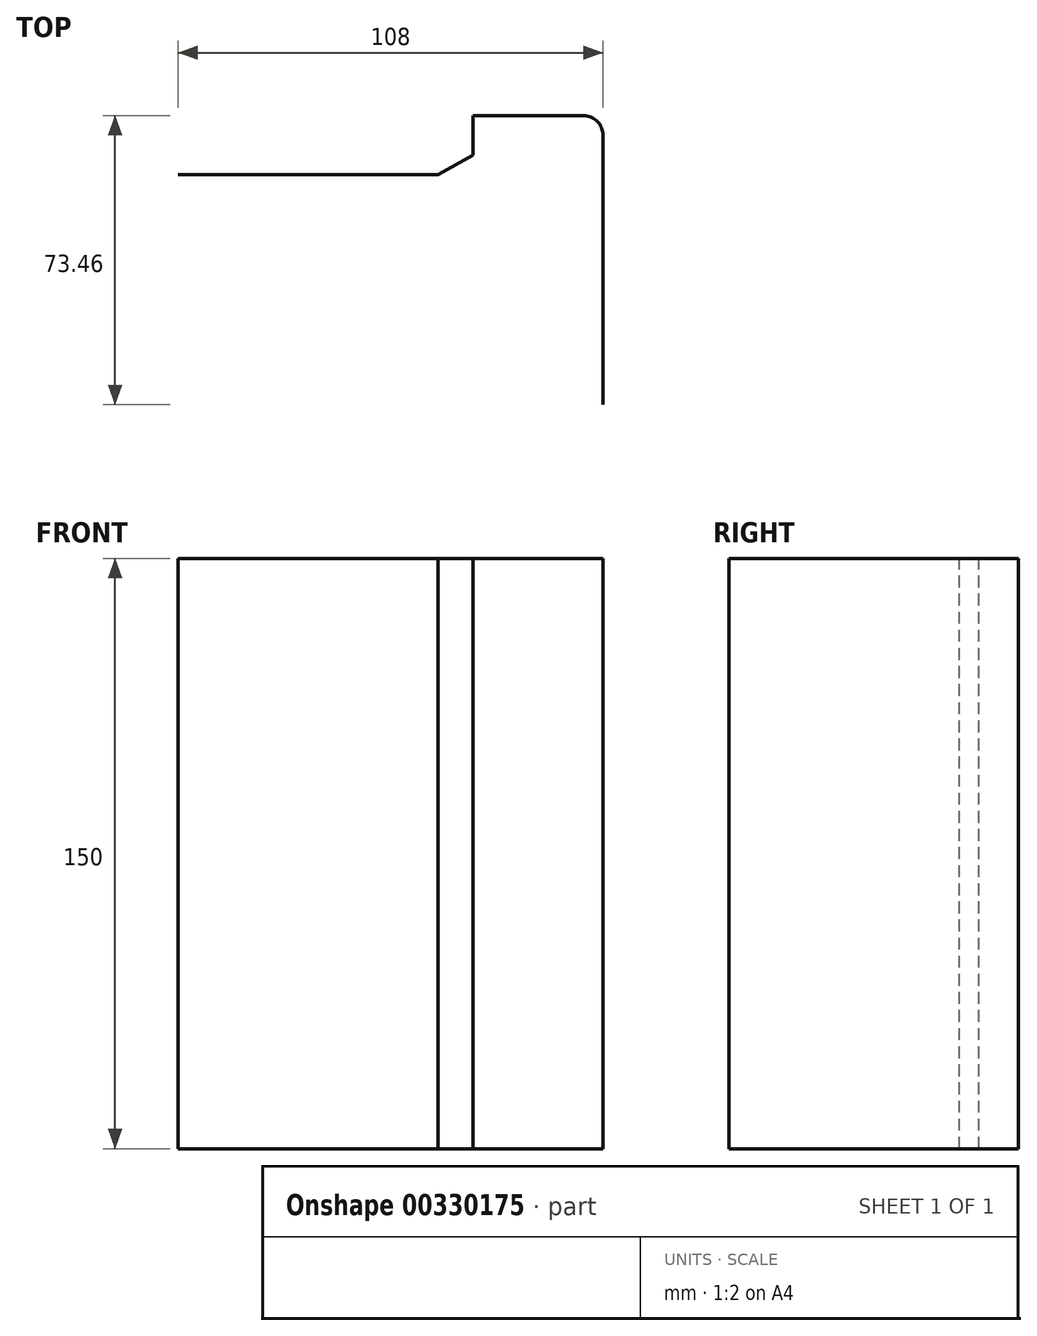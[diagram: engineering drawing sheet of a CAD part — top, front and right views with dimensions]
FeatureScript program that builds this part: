
annotation { "Feature Type Name" : "Feature", "Feature Type Description" : "" }
export const myFeature = defineFeature(function(context is Context, id is Id, definition is map)
    precondition{}
    {
        {
            var Q0;
            Q0=qCreatedBy(makeId("Top.planeOp"),FACE);
            var sketch = newSketch(context, id + "F0", { "sketchPlane" : qUnion([Q0])});
            skLineSegment(sketch, "E0", {"start": v(0, 0) * mm, "end": v(28, 0) * mm});
            skLineSegment(sketch, "E1", {"start": v(33, -5) * mm, "end": v(33, -73.46) * mm});
            skLineSegment(sketch, "E2", {"start": v(0, 0) * mm, "end": v(0, -10) * mm});
            skLineSegment(sketch, "E3", {"start": v(0, -10) * mm, "end": v(-9, -15) * mm});
            skLineSegment(sketch, "E4", {"start": v(-9, -15) * mm, "end": v(-75, -15) * mm});
            skPoint(sketch, "E5.visualSharp", {"position": v(33, 0) * mm});
            skArc(sketch, "E5.filletArc", {"start": v(33, -5) * mm, "mid": v(31.54, -1.46) * mm, "end": v(28, 0) * mm});
            skSolve(sketch);
        }
        {
            var Q0;
            Q0=sQuery(id+"F0.wireOp",EDGE,"E4");
            var Q1;
            Q1=sQuery(id+"F0.wireOp",EDGE,"E0");
            var Q2;
            Q2=sQuery(id+"F0.wireOp",EDGE,"E3");
            var Q3;
            Q3=sQuery(id+"F0.wireOp",EDGE,"E1");
            var Q4;
            Q4=sQuery(id+"F0.wireOp",EDGE,"E2");
            var Q5;
            Q5=sQuery(id+"F0.wireOp",EDGE,"E5.filletArc");
            extrude(context, id + "F1", {"bodyType" : ToolBodyType.SURFACE, "surfaceEntities" : qUnion([Q0, Q1, Q2, Q3, Q4, Q5]), "endBound" : BoundingType.SYMMETRIC, "depth" : 150 * mm});
        }
    });
